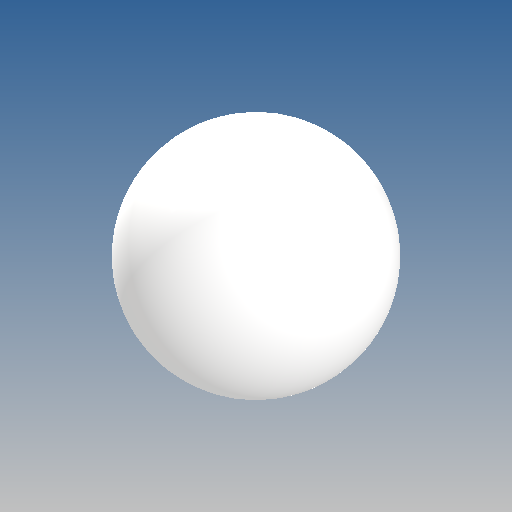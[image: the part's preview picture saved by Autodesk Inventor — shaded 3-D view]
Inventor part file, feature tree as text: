
AUTODESK INVENTOR PART (.ipt)
format: ipt  version: 2025 (Build 290162010, 162A)  size: 118,784 bytes
history: native  units: mm
features: revolve x1, sketch x1
ambient origin geometry x8: Origin, YZ Plane, XZ Plane, XY Plane, X Axis, Y Axis, Z Axis, Center Point
bodies: Volumenkörper1 (feature_tree)
feature tree (2):
  revolve  "Umdrehung1"
  sketch  "Skizze1"  dims[d0=19.0mm d1=360.0deg]
